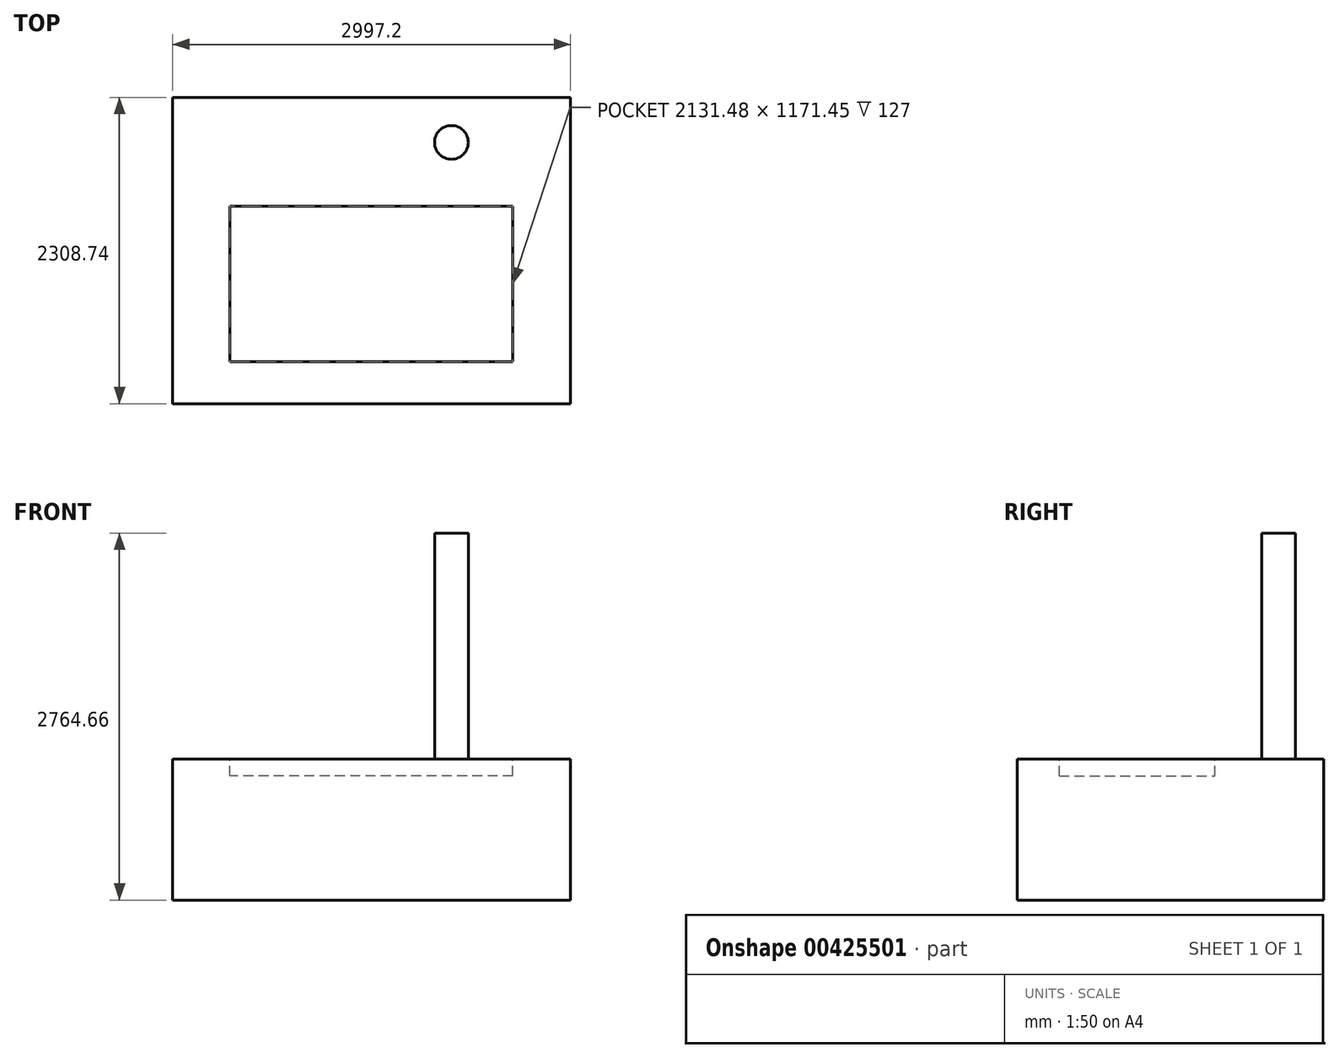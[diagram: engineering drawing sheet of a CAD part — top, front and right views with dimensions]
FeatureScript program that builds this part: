
annotation { "Feature Type Name" : "Feature", "Feature Type Description" : "" }
export const myFeature = defineFeature(function(context is Context, id is Id, definition is map)
    precondition{}
    {
        {
            var Q0;
            Q0=qCreatedBy(makeId("Top.planeOp"),FACE);
            var sketch = newSketch(context, id + "F0", { "sketchPlane" : qUnion([Q0])});
            skLineSegment(sketch, "E0.bottom", {"start": v(1498.6, -902.2) * mm, "end": v(-1498.6, -902.2) * mm});
            skLineSegment(sketch, "E0.top", {"start": v(1498.6, 1406.53) * mm, "end": v(-1498.6, 1406.53) * mm});
            skLineSegment(sketch, "E0.left", {"start": v(1498.6, -902.2) * mm, "end": v(1498.6, 1406.53) * mm});
            skLineSegment(sketch, "E0.right", {"start": v(-1498.6, -902.2) * mm, "end": v(-1498.6, 1406.53) * mm});
            skPoint(sketch, "E0.middle", {"position": v(0, 252.16) * mm});
            skSolve(sketch);
        }
        {
            var Q0;
            Q0=makeQuery(id+"F0.imprint","IMPRINT",FACE,{"disambiguationData":[TD([[makeQuery(id+"F0.imprint","IMPRINT",EDGE,{"derivedFrom":sQuery(id+"F0.wireOp",EDGE,"E0.bottom")}),-1.0]])]});
            extrude(context, id + "F1", {"entities" : qUnion([Q0]), "depth" : 226.06 * mm});
        }
        {
            var Q0;
            Q0=makeQuery(id+"F1.opExtrude","CAP_FACE",FACE,{"disambiguationData":[OSD([sQuery(id+"F0.wireOp",EDGE,"E0.bottom"),sQuery(id+"F0.wireOp",EDGE,"E0.top"),sQuery(id+"F0.wireOp",EDGE,"E0.left"),sQuery(id+"F0.wireOp",EDGE,"E0.right")])],"isStart":false});
            var sketch = newSketch(context, id + "F2", { "sketchPlane" : qUnion([Q0])});
            skLineSegment(sketch, "E1.bottom", {"start": v(1063.53, -585.72) * mm, "end": v(-1067.94, -585.72) * mm});
            skLineSegment(sketch, "E1.top", {"start": v(1063.53, 585.72) * mm, "end": v(-1067.94, 585.72) * mm});
            skLineSegment(sketch, "E1.left", {"start": v(1063.53, -585.72) * mm, "end": v(1063.53, 585.72) * mm});
            skLineSegment(sketch, "E1.right", {"start": v(-1067.94, -585.72) * mm, "end": v(-1067.94, 585.72) * mm});
            skPoint(sketch, "E1.middle", {"position": v(-2.2, 0) * mm});
            skSolve(sketch);
        }
        {
            var Q0;
            Q0 = qSketchRegion(id + "F2", true);
            extrude(context, id + "F3", {"entities" : qUnion([Q0]), "operationType" : NewBodyOperationType.REMOVE, "oppositeDirection" : true, "depth" : 127 * mm});
        }
        {
            var Q0;
            Q0=makeQuery(id+"F1.opExtrude","CAP_FACE",FACE,{"disambiguationData":[OSD([sQuery(id+"F0.wireOp",EDGE,"E0.bottom"),sQuery(id+"F0.wireOp",EDGE,"E0.top"),sQuery(id+"F0.wireOp",EDGE,"E0.left"),sQuery(id+"F0.wireOp",EDGE,"E0.right")])],"isStart":false});
            var sketch = newSketch(context, id + "F4", { "sketchPlane" : qUnion([Q0])});
            skCircle(sketch, "E2", {"center": v(601.01, 1066.93) * mm, "radius": 127 * mm});
            skSolve(sketch);
        }
        {
            var Q0;
            Q0=makeQuery(id+"F4.imprint","IMPRINT",FACE,{"disambiguationData":[TD([[makeQuery(id+"F4.imprint","IMPRINT",EDGE,{"derivedFrom":sQuery(id+"F4.wireOp",EDGE,"E2")}),1.0]])]});
            extrude(context, id + "F5", {"entities" : qUnion([Q0]), "operationType" : NewBodyOperationType.ADD, "depth" : 1701.8 * mm});
        }
        {
            var Q0;
            Q0=makeQuery(id+"F1.opExtrude","SWEPT_FACE",FACE,{"disambiguationData":[OSD([sQuery(id+"F0.wireOp",EDGE,"E0.bottom")])]});
            var sketch = newSketch(context, id + "F6", { "sketchPlane" : qUnion([Q0])});
            skLineSegment(sketch, "E3.bottom", {"start": v(-1498.6, 0) * mm, "end": v(1498.6, 0) * mm});
            skLineSegment(sketch, "E3.top", {"start": v(-1498.6, -836.8) * mm, "end": v(1498.6, -836.8) * mm});
            skLineSegment(sketch, "E3.left", {"start": v(-1498.6, 0) * mm, "end": v(-1498.6, -836.8) * mm});
            skLineSegment(sketch, "E3.right", {"start": v(1498.6, 0) * mm, "end": v(1498.6, -836.8) * mm});
            skSolve(sketch);
        }
        {
            var Q0;
            Q0 = qSketchRegion(id + "F6", true);
            extrude(context, id + "F7", {"entities" : qUnion([Q0]), "operationType" : NewBodyOperationType.ADD, "oppositeDirection" : true, "depth" : 2308.74 * mm});
        }
    });
